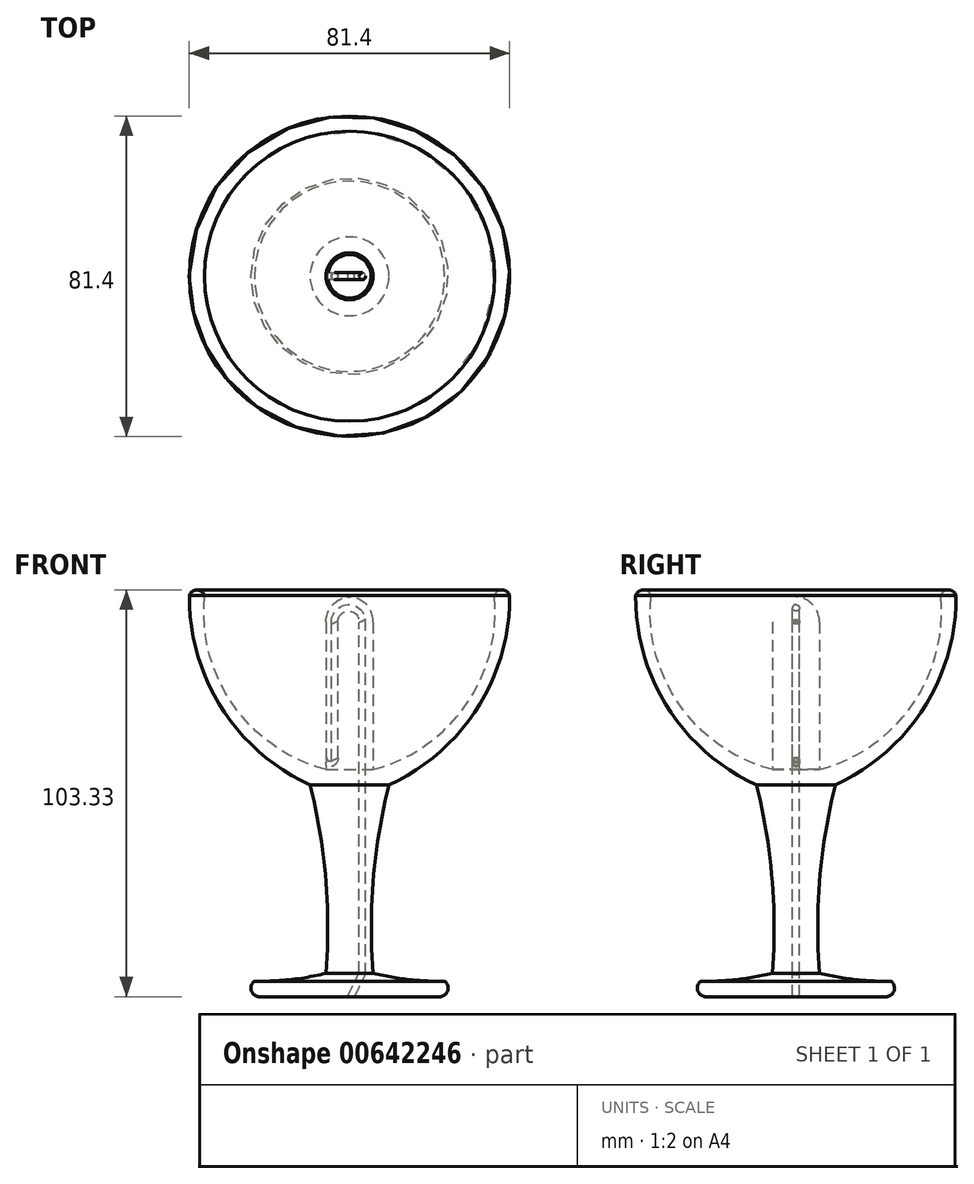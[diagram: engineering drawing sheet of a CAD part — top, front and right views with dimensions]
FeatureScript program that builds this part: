
annotation { "Feature Type Name" : "Feature", "Feature Type Description" : "" }
export const myFeature = defineFeature(function(context is Context, id is Id, definition is map)
    precondition{}
    {
        {
            var Q0;
            Q0=qCreatedBy(makeId("Front.planeOp"),FACE);
            var sketch = newSketch(context, id + "F0", { "sketchPlane" : qUnion([Q0])});
            skLineSegment(sketch, "E0", {"start": v(0, 0) * mm, "end": v(0, 101.6) * mm});
            skLineSegment(sketch, "E1", {"start": v(0, 0) * mm, "end": v(-22.86, 0) * mm});
            skArc(sketch, "E2", {"start": v(-24.17, 3.93) * mm, "mid": v(-24.93, 1.5) * mm, "end": v(-22.86, 0) * mm});
            skArc(sketch, "E3", {"start": v(-24.17, 3.93) * mm, "mid": v(-15, 4.34) * mm, "end": v(-5.98, 5.95) * mm});
            skArc(sketch, "E4", {"start": v(-5.98, 5.95) * mm, "mid": v(-6.06, 30.05) * mm, "end": v(-10.02, 53.82) * mm});
            skArc(sketch, "E5", {"start": v(-40.7, 101.87) * mm, "mid": v(-32.47, 73.3) * mm, "end": v(-10.02, 53.82) * mm});
            skArc(sketch, "E6", {"start": v(-36.84, 101.87) * mm, "mid": v(-38.77, 103.33) * mm, "end": v(-40.7, 101.87) * mm});
            skArc(sketch, "E7", {"start": v(-36.84, 101.87) * mm, "mid": v(-29.54, 74.1) * mm, "end": v(-5.98, 57.69) * mm});
            skLineSegment(sketch, "E8", {"start": v(-5.98, 57.69) * mm, "end": v(-5.98, 95.25) * mm});
            skLineSegment(sketch, "E9", {"start": v(-5.98, 95.25) * mm, "end": v(-5.98, 57.69) * mm});
            skArc(sketch, "E10", {"start": v(0, 101.6) * mm, "mid": v(-4.25, 99.61) * mm, "end": v(-5.98, 95.25) * mm});
            skSolve(sketch);
        }
        {
            var Q0;
            Q0=makeQuery(id+"F0.imprint","IMPRINT",FACE,{"disambiguationData":[TD([[makeQuery(id+"F0.imprint","IMPRINT",EDGE,{"derivedFrom":sQuery(id+"F0.wireOp",EDGE,"E0")}),1.0]])]});
            var Q1;
            Q1=sQuery(id+"F0.wireOp",EDGE,"E0");
            revolve(context, id + "F1", {"entities" : qUnion([Q0]), "axis" : qUnion([Q1]), "revolveType" : RevolveType.FULL});
        }
        {
            var Q0;
            Q0=qCreatedBy(makeId("Front.planeOp"),FACE);
            var sketch = newSketch(context, id + "F2", { "sketchPlane" : qUnion([Q0])});
            skLineSegment(sketch, "E11", {"start": v(-0.01, 0) * mm, "end": v(-0.01, 101.6) * mm});
            skLineSegment(sketch, "E12", {"start": v(-0.01, 0) * mm, "end": v(-22.87, 0) * mm});
            skArc(sketch, "E13", {"start": v(-24.19, 3.93) * mm, "mid": v(-24.94, 1.5) * mm, "end": v(-22.87, 0) * mm});
            skArc(sketch, "E14", {"start": v(-24.19, 3.93) * mm, "mid": v(-15.02, 4.34) * mm, "end": v(-6, 5.95) * mm});
            skArc(sketch, "E15", {"start": v(-6, 5.95) * mm, "mid": v(-6.08, 30.05) * mm, "end": v(-10.04, 53.82) * mm});
            skArc(sketch, "E16", {"start": v(-40.7, 101.87) * mm, "mid": v(-32.49, 73.3) * mm, "end": v(-10.04, 53.82) * mm});
            skArc(sketch, "E17", {"start": v(-36.85, 101.87) * mm, "mid": v(-38.78, 103.33) * mm, "end": v(-40.7, 101.87) * mm});
            skArc(sketch, "E18", {"start": v(-36.85, 101.87) * mm, "mid": v(-29.55, 74.1) * mm, "end": v(-6, 57.69) * mm});
            skLineSegment(sketch, "E19", {"start": v(-6, 57.69) * mm, "end": v(-6, 95.25) * mm});
            skLineSegment(sketch, "E20", {"start": v(-6, 95.25) * mm, "end": v(-6, 57.69) * mm});
            skArc(sketch, "E21", {"start": v(-0.01, 101.6) * mm, "mid": v(-4.26, 99.61) * mm, "end": v(-6, 95.25) * mm});
            skArc(sketch, "E22.MirrorCS", {"start": v(-0.01, 101.6) * mm, "mid": v(4.24, 99.61) * mm, "end": v(5.97, 95.25) * mm});
            skLineSegment(sketch, "E23.MirrorCS", {"start": v(5.97, 95.25) * mm, "end": v(5.97, 57.69) * mm});
            skArc(sketch, "E24.MirrorCS", {"start": v(5.97, 5.95) * mm, "mid": v(6.05, 30.05) * mm, "end": v(10.01, 53.82) * mm});
            skArc(sketch, "E25.MirrorCS", {"start": v(24.16, 3.93) * mm, "mid": v(15, 4.34) * mm, "end": v(5.97, 5.95) * mm});
            skLineSegment(sketch, "E26.MirrorCS", {"start": v(-0.01, 0) * mm, "end": v(22.85, 0) * mm});
            skArc(sketch, "E27.MirrorCS", {"start": v(24.16, 3.93) * mm, "mid": v(24.92, 1.5) * mm, "end": v(22.85, 0) * mm});
            skArc(sketch, "E28.MirrorCS", {"start": v(40.69, 101.87) * mm, "mid": v(32.46, 73.3) * mm, "end": v(10.01, 53.82) * mm});
            skArc(sketch, "E29.MirrorCS", {"start": v(36.83, 101.87) * mm, "mid": v(29.53, 74.1) * mm, "end": v(5.97, 57.69) * mm});
            skArc(sketch, "E30.MirrorCS", {"start": v(36.83, 101.87) * mm, "mid": v(38.76, 103.33) * mm, "end": v(40.69, 101.87) * mm});
            skLineSegment(sketch, "E31", {"start": v(0, 0) * mm, "end": v(2.91, 5.9) * mm});
            skLineSegment(sketch, "E32", {"start": v(2.91, 5.9) * mm, "end": v(2.91, 95.25) * mm});
            skLineSegment(sketch, "E33", {"start": v(-3.42, 95.25) * mm, "end": v(-3.42, 60.47) * mm});
            skArc(sketch, "E34", {"start": v(2.91, 95.25) * mm, "mid": v(-0.25, 98.42) * mm, "end": v(-3.42, 95.25) * mm});
            skArc(sketch, "E35", {"start": v(-6, 59.33) * mm, "mid": v(-4.33, 59.07) * mm, "end": v(-3.42, 60.47) * mm});
            skSolve(sketch);
        }
        {
            var Q0;
            Q0=qCreatedBy(makeId("Top.planeOp"),FACE);
            var sketch = newSketch(context, id + "F3", { "sketchPlane" : qUnion([Q0])});
            skCircle(sketch, "E36", {"center": v(0.38, 0) * mm, "radius": 0.89 * mm});
            skSolve(sketch);
        }
        {
            var Q0;
            Q0=makeQuery(id+"F3.imprint","IMPRINT",FACE,{"disambiguationData":[TD([[makeQuery(id+"F3.imprint","IMPRINT",EDGE,{"derivedFrom":sQuery(id+"F3.wireOp",EDGE,"E36")}),1.0]])]});
            var Q1;
            Q1=sQuery(id+"F2.wireOp",EDGE,"E31");
            var Q2;
            Q2=sQuery(id+"F2.wireOp",EDGE,"E32");
            var Q3;
            Q3=sQuery(id+"F2.wireOp",EDGE,"E34");
            var Q4;
            Q4=sQuery(id+"F2.wireOp",EDGE,"E33");
            var Q5;
            Q5=sQuery(id+"F2.wireOp",EDGE,"E35");
            sweep(context, id + "F4", {"profiles" : qUnion([Q0]), "path" : qUnion([Q1, Q2, Q3, Q4, Q5])});
        }
        {
            var Q0;
            Q0=makeQuery(id+"F4.opSweep","SWEPT_BODY",BODY,{"disambiguationData":[OSD([sQuery(id+"F2.wireOp",EDGE,"E35"),sQuery(id+"F3.wireOp",EDGE,"E36")])]});
            var Q1;
            Q1=makeQuery(id+"F1.opRevolve","SWEPT_BODY",BODY,{"disambiguationData":[OSD([sQuery(id+"F0.wireOp",EDGE,"E0"),sQuery(id+"F0.wireOp",EDGE,"E1"),sQuery(id+"F0.wireOp",EDGE,"E2"),sQuery(id+"F0.wireOp",EDGE,"E3"),sQuery(id+"F0.wireOp",EDGE,"E4"),sQuery(id+"F0.wireOp",EDGE,"E5"),sQuery(id+"F0.wireOp",EDGE,"E6"),sQuery(id+"F0.wireOp",EDGE,"E7"),sQuery(id+"F0.wireOp",EDGE,"E9"),sQuery(id+"F0.wireOp",EDGE,"E10")])]});
            booleanBodies(context, id + "F5", {"operationType" : BooleanOperationType.SUBTRACTION, "tools" : qUnion([Q0]), "targets" : qUnion([Q1])});
        }
    });
